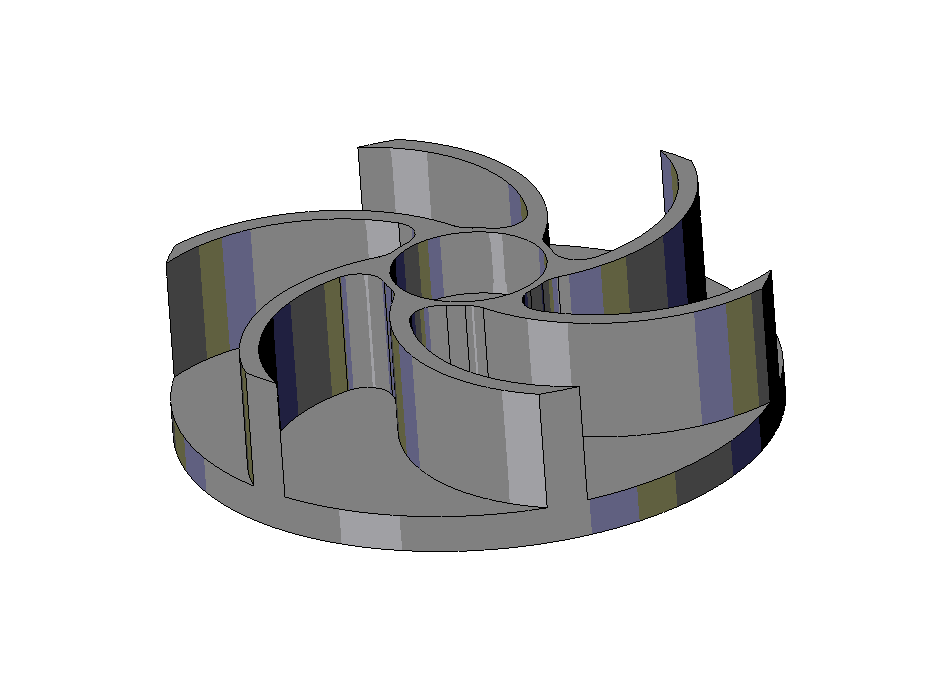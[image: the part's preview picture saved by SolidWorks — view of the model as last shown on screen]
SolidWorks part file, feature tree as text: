
SOLIDWORKS PART (.sldprt)
format: sldprt  version: not decoded by parser v0  size: 858,112 bytes
history: native  units: mm
features: sketch x7, extrude x5, pattern_circular x2, material x1, hole x1 (+12 scaffold rows collapsed)
feature tree (28):
  scaffold x12  (default folders/planes/origin — collapsed)
  material  "Material <not specified>"
  sketch  "Sketch1"  dims[D1=63.0mm]
  extrude  "Extrude1"  Depth=4mm
  sketch  "Sketch2"  dims[c1.D1=18.0mm c1.D2=70.0mm c1.D3=40.0mm c1.D4=20.0mm c2.D3=20.0mm c2.D2=19.0mm c3.D3=21.0mm c3.D4=20.0mm c3.D5=~28.160342mm c3.D6=20.0mm c3.D7=20.0mm c3.D2=3.0mm c3.D1=9.0mm c4.D3=11.0mm c4.D1=18.0mm c4.D4=5.5mm c5.D3=3.0mm c5.D4=12.0mm c5.D5=12.0mm c5.D6=8.0mm c6.D5=35.0mm c6.D2=2.0mm c6.D3=40.0mm c7.D5=~20.295395mm c8.D5=35.0deg c8.D4=3.5mm c8.D3=~4.075917mm c8.D2=1.0mm c9.D3=1.0mm c9.D7=1.0mm c9.D8=1.0mm]
  sketch  "Sketch3"  dims[D1=18.0mm]
  extrude  "Extrude2"  Depth=10mm
  hole  "M11.0 (11) Diameter Hole1"  Diameter=11mm Depth=10mm
  sketch  "Sketch5"
  sketch  "Sketch4"  dims[hole-wizard template sketch: 47 standard entries collapsed; hole parameters kept: c15.Hole Depth=10.0mm c15.D3=~14.816244mm c15.Drill Angle=118.0deg]
  extrude  "Extrude3"  Depth=13mm
  pattern_circular  "CirPattern1"  Count=4 Angle=360deg
  extrude  "Extrude4"  [1 undecoded]
  sketch  "Sketch2<8>"  dims[D1=13.0mm]
  pattern_circular  "CirPattern2"  Count=6 Angle=360deg
  sketch  "Sketch7"  dims[D1=16.2mm D2=18.0mm]
  extrude  "Extrude5"  [1 undecoded]
decode coverage: 12 of 15 modeling features carry decoded parameters
note: ~ marks probable driven/reference dimensions
note: 2 parameter values undecoded
note: suppression state not decoded; provenance and decode notes live in map.json
